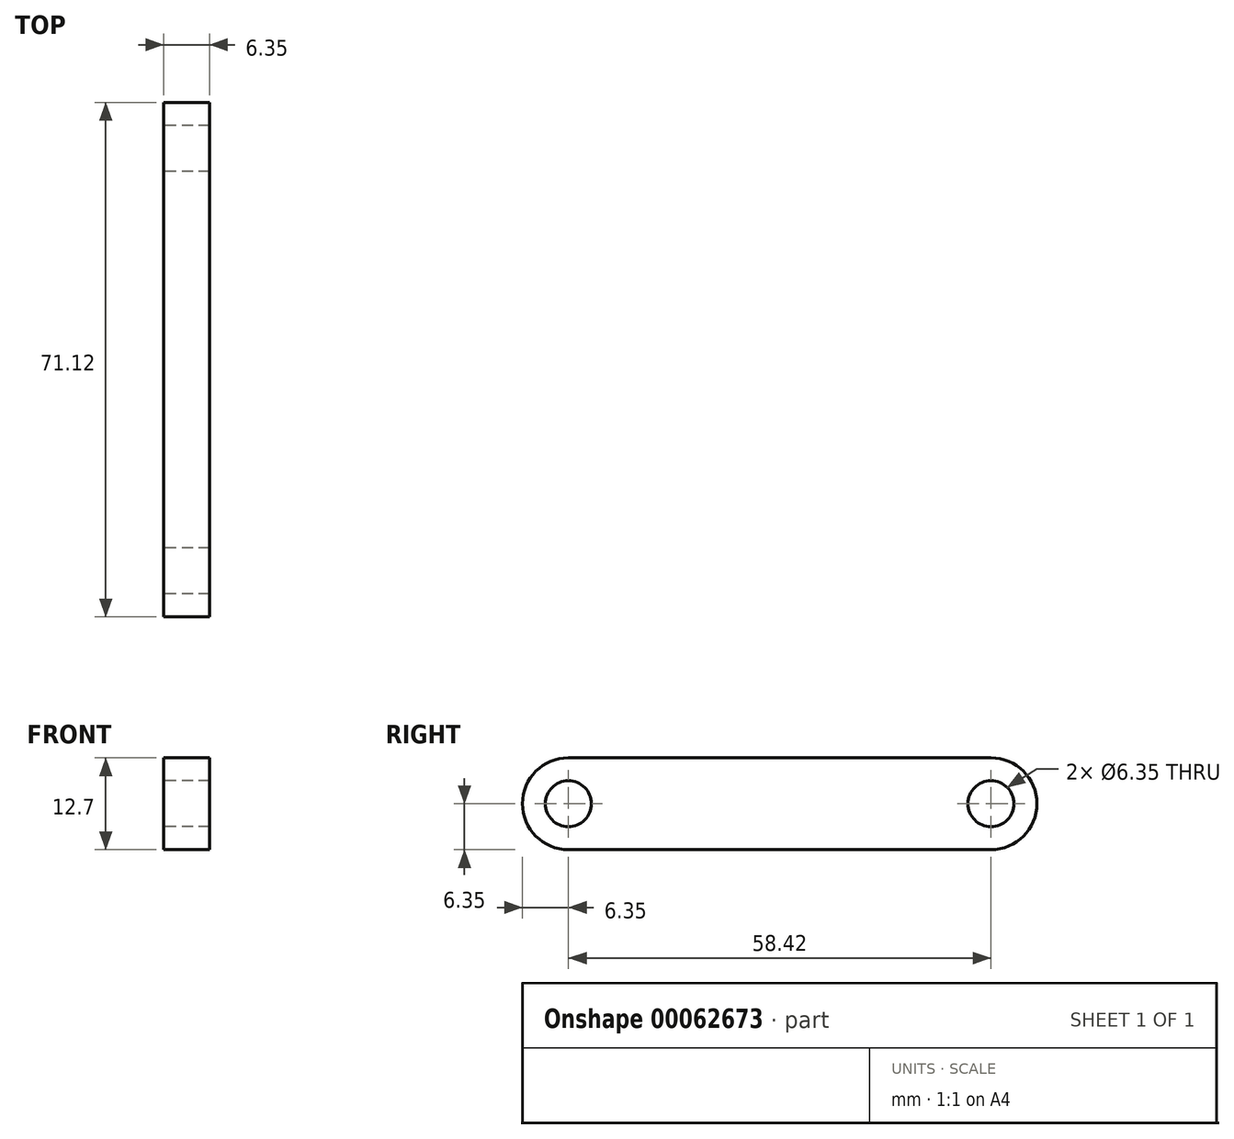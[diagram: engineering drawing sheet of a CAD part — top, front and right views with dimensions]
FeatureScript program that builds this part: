
annotation { "Feature Type Name" : "Feature", "Feature Type Description" : "" }
export const myFeature = defineFeature(function(context is Context, id is Id, definition is map)
    precondition{}
    {
        {
            var Q0;
            Q0=qCreatedBy(makeId("Right.planeOp"),FACE);
            var sketch = newSketch(context, id + "F0", { "sketchPlane" : qUnion([Q0])});
            skCircle(sketch, "E0", {"center": v(0, 0) * mm, "radius": 3.18 * mm});
            skArc(sketch, "E1", {"start": v(0, 6.35) * mm, "mid": v(-6.35, 0) * mm, "end": v(0, -6.35) * mm});
            skArc(sketch, "E2", {"start": v(58.42, -6.35) * mm, "mid": v(64.77, 0) * mm, "end": v(58.42, 6.35) * mm});
            skCircle(sketch, "E3", {"center": v(58.42, 0) * mm, "radius": 3.18 * mm});
            skLineSegment(sketch, "E4", {"start": v(0, 6.35) * mm, "end": v(58.42, 6.35) * mm});
            skLineSegment(sketch, "E5", {"start": v(0, -6.35) * mm, "end": v(58.42, -6.35) * mm});
            skSolve(sketch);
        }
        {
            var Q0;
            Q0=makeQuery(id+"F0.imprint","IMPRINT",FACE,{"disambiguationData":[TD([[makeQuery(id+"F0.imprint","IMPRINT",EDGE,{"derivedFrom":sQuery(id+"F0.wireOp",EDGE,"E0")}),-1.0]])]});
            extrude(context, id + "F1", {"entities" : qUnion([Q0]), "depth" : 6.35 * mm});
        }
    });
